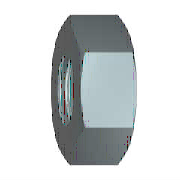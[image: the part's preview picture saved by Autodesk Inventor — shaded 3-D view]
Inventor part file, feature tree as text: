
AUTODESK INVENTOR PART (.ipt)
format: ipt  version: 2015 (Build 190159000, 159)  size: 162,816 bytes
history: native  units: mm (DEFAULTED — no unit token found)
features: sketch x3, chamfer x1, hole x1, other x1, plane x1
ambient origin geometry x7: Origin, YZ Plane, XZ Plane, X Axis, Y Axis, Z Axis, Center Point
bodies: Solid1 (feature_tree), Body (feature_tree)
feature tree (7):
  chamfer  "Chamfer1"  Angle=30.0deg  [1 undecoded]
  hole  "Thread"  [1 undecoded]
  other  "Work Axis1"
  plane  "Work Plane1"
  sketch  "Sketch1"  dims[d0=6.350853mm]
  sketch  "Sketch2"  dims[d1=2.4mm]
  sketch  "Sketch3"  dims[d2=0.0mm d3=30.0deg d4=30.0deg d5=4.6mm d6=4.6mm d7=90.0deg d25=2.459mm d26=6.0mm d27=4.0mm d28=2.0mm d29=14.3117mm d30=8.0mm d31=20.594885mm d8=0.270633mm d9=30.0deg d10=0.270633mm d11=30.0deg d13=0.0mm d14=0.0mm d39=0.0mm d40=0.270633mm d41=0.270633mm d42=0.0mm]
note: 2 required parameter values undecoded (feature->parameter linkage not recoverable at this tier; creation-order binding heuristic only, values carry confidence <= 0.55)
